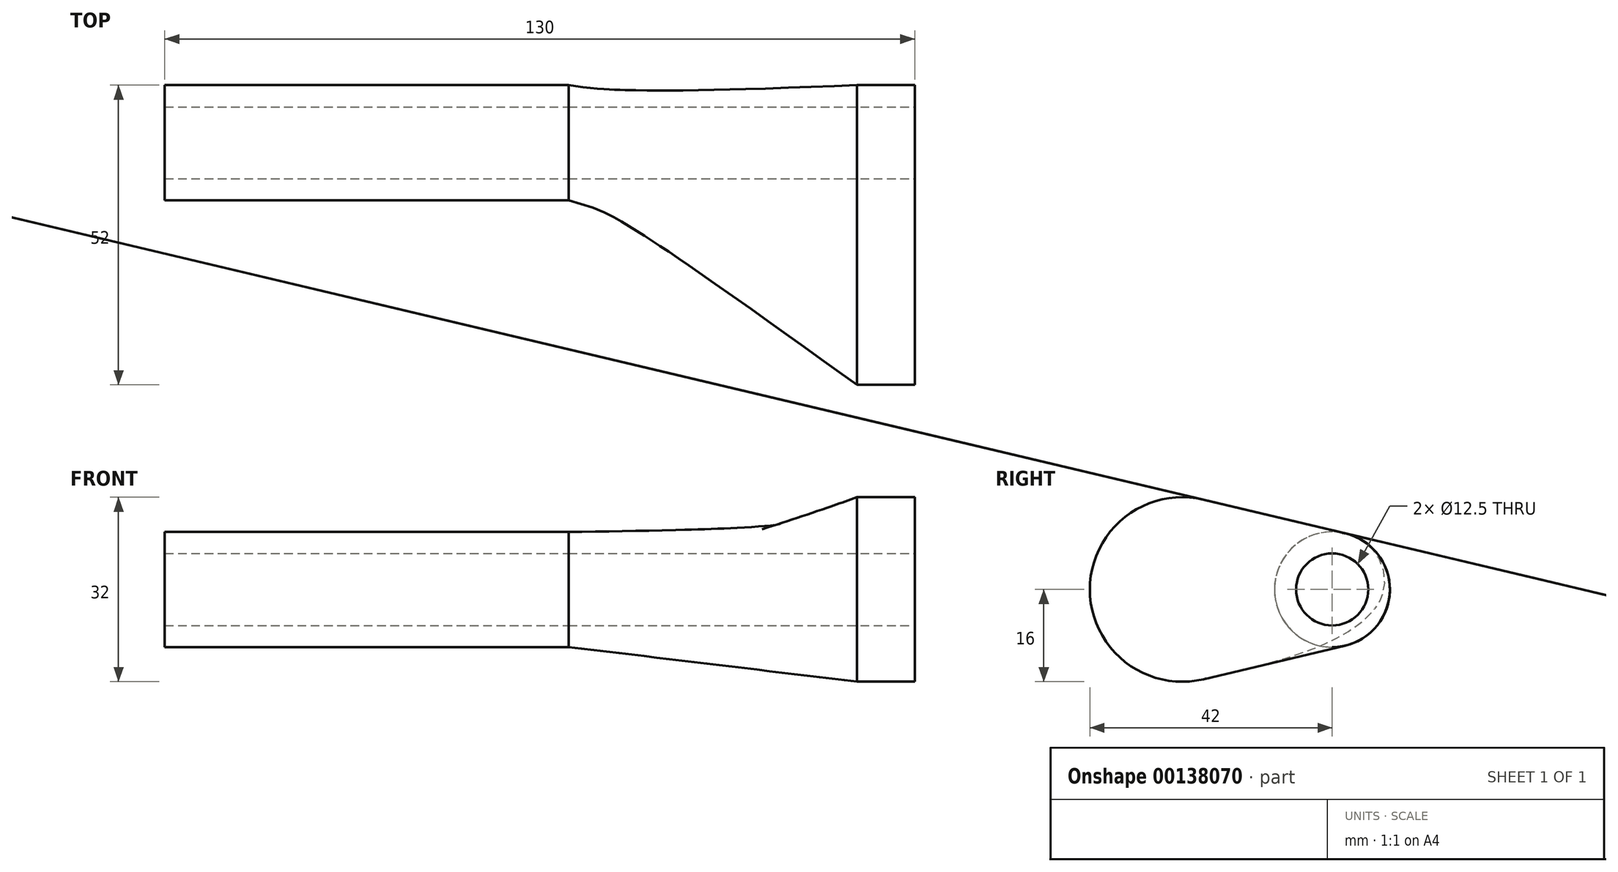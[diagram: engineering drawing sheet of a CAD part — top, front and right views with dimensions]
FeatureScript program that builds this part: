
annotation { "Feature Type Name" : "Feature", "Feature Type Description" : "" }
export const myFeature = defineFeature(function(context is Context, id is Id, definition is map)
    precondition{}
    {
        {
            var Q0;
            Q0=qCreatedBy(makeId("Right.planeOp"),FACE);
            var sketch = newSketch(context, id + "F0", { "sketchPlane" : qUnion([Q0])});
            skArc(sketch, "E0", {"start": v(2.3, -9.73) * mm, "mid": v(10, 0) * mm, "end": v(2.3, 9.73) * mm});
            skArc(sketch, "E1", {"start": v(-22.3, 15.57) * mm, "mid": v(-42, 0) * mm, "end": v(-22.3, -15.57) * mm});
            skLineSegment(sketch, "E2", {"start": v(2.3, 9.73) * mm, "end": v(-22.3, 15.57) * mm});
            skLineSegment(sketch, "E3", {"start": v(2.3, -9.73) * mm, "end": v(-22.3, -15.57) * mm});
            skSolve(sketch);
        }
        {
            var Q0;
            Q0=qCreatedBy(makeId("Right.planeOp"),FACE);
            cPlane(context, id + "F1", {"entities" : qUnion([Q0]), "cplaneType" : CPlaneType.OFFSET, "offset" : 130 * mm, "oppositeDirection" : true, "width" : 150 * mm, "height" : 150 * mm});
        }
        {
            var Q0;
            Q0=qCreatedBy(makeId("Right.planeOp"),FACE);
            cPlane(context, id + "F2", {"entities" : qUnion([Q0]), "cplaneType" : CPlaneType.OFFSET, "offset" : 10 * mm, "oppositeDirection" : true, "width" : 150 * mm, "height" : 150 * mm});
        }
        {
            var Q0;
            Q0=qCreatedBy(id+"F1.planeOp",FACE);
            cPlane(context, id + "F3", {"entities" : qUnion([Q0]), "cplaneType" : CPlaneType.OFFSET, "offset" : 70 * mm, "width" : 150 * mm, "height" : 150 * mm});
        }
        {
            var Q0;
            Q0=qCreatedBy(id+"F2.planeOp",FACE);
            var sketch = newSketch(context, id + "F4", { "sketchPlane" : qUnion([Q0])});
            skLineSegment(sketch, "E4.0.0", {"start": v(-22.3, -15.57) * mm, "end": v(2.3, -9.73) * mm});
            skArc(sketch, "E4.0.1", {"start": v(2.3, -9.73) * mm, "mid": v(10, 0) * mm, "end": v(2.3, 9.73) * mm});
            skLineSegment(sketch, "E4.0.2", {"start": v(2.3, 9.73) * mm, "end": v(-22.3, 15.57) * mm});
            skArc(sketch, "E4.0.3", {"start": v(-22.3, 15.57) * mm, "mid": v(-42, 0) * mm, "end": v(-22.3, -15.57) * mm});
            skSolve(sketch);
        }
        {
            var Q0;
            Q0=qCreatedBy(id+"F3.planeOp",FACE);
            var sketch = newSketch(context, id + "F5", { "sketchPlane" : qUnion([Q0])});
            skArc(sketch, "E5", {"start": v(2.33, 9.72) * mm, "mid": v(-10, 0.05) * mm, "end": v(2.22, -9.75) * mm});
            skArc(sketch, "E6", {"start": v(2.22, -9.75) * mm, "mid": v(10, -0.05) * mm, "end": v(2.33, 9.72) * mm});
            skSolve(sketch);
        }
        {
            var Q0;
            Q0=qCreatedBy(id+"F1.planeOp",FACE);
            var sketch = newSketch(context, id + "F6", { "sketchPlane" : qUnion([Q0])});
            skArc(sketch, "E7.0.0", {"start": v(2.22, -9.75) * mm, "mid": v(10, -0.05) * mm, "end": v(2.33, 9.72) * mm});
            skArc(sketch, "E7.0.1", {"start": v(2.33, 9.72) * mm, "mid": v(-10, 0.05) * mm, "end": v(2.22, -9.75) * mm});
            skSolve(sketch);
        }
        {
            var Q0;
            Q0 = qSketchRegion(id + "F5", true);
            var Q1;
            Q1 = qSketchRegion(id + "F4", true);
            loft(context, id + "F7", {"sheetProfilesArray" : [{ "sheetProfileEntities" : qUnion([Q0]) }, { "sheetProfileEntities" : qUnion([Q1]) }]});
        }
        {
            var Q1;
            Q1 = qSketchRegion(id + "F4", true);
            var Q2;
            Q2 = qSketchRegion(id + "F0", true);
            loft(context, id + "F8", {"operationType" : NewBodyOperationType.ADD, "sheetProfilesArray" : [{ "sheetProfileEntities" : qUnion([Q1]) }, { "sheetProfileEntities" : qUnion([Q2]) }]});
        }
        {
            var Q0;
            Q0 = qSketchRegion(id + "F6", true);
            var Q1;
            Q1 = qSketchRegion(id + "F5", true);
            loft(context, id + "F9", {"sheetProfilesArray" : [{ "sheetProfileEntities" : qUnion([Q0]) }, { "sheetProfileEntities" : qUnion([Q1]) }]});
        }
        {
            var Q0;
            Q0=qCreatedBy(makeId("Right.planeOp"),FACE);
            var sketch = newSketch(context, id + "F10", { "sketchPlane" : qUnion([Q0])});
            skCircle(sketch, "E8", {"center": v(0, 0) * mm, "radius": 6.25 * mm});
            skSolve(sketch);
        }
        {
            var Q0;
            Q0 = qSketchRegion(id + "F10", true);
            extrude(context, id + "F11", {"entities" : qUnion([Q0]), "operationType" : NewBodyOperationType.REMOVE, "endBound" : BoundingType.THROUGH_ALL, "oppositeDirection" : true, "depth" : 25 * mm});
        }
        {
            var Q0;
            Q0=qCreatedBy(id+"F1.planeOp",FACE);
            var sketch = newSketch(context, id + "F12", { "sketchPlane" : qUnion([Q0])});
            skCircle(sketch, "E9", {"center": v(0, 0) * mm, "radius": 6.25 * mm});
            skSolve(sketch);
        }
        {
            var Q0;
            Q0 = qSketchRegion(id + "F12", true);
            extrude(context, id + "F13", {"entities" : qUnion([Q0]), "operationType" : NewBodyOperationType.REMOVE, "endBound" : BoundingType.THROUGH_ALL, "depth" : 25 * mm});
        }
    });
